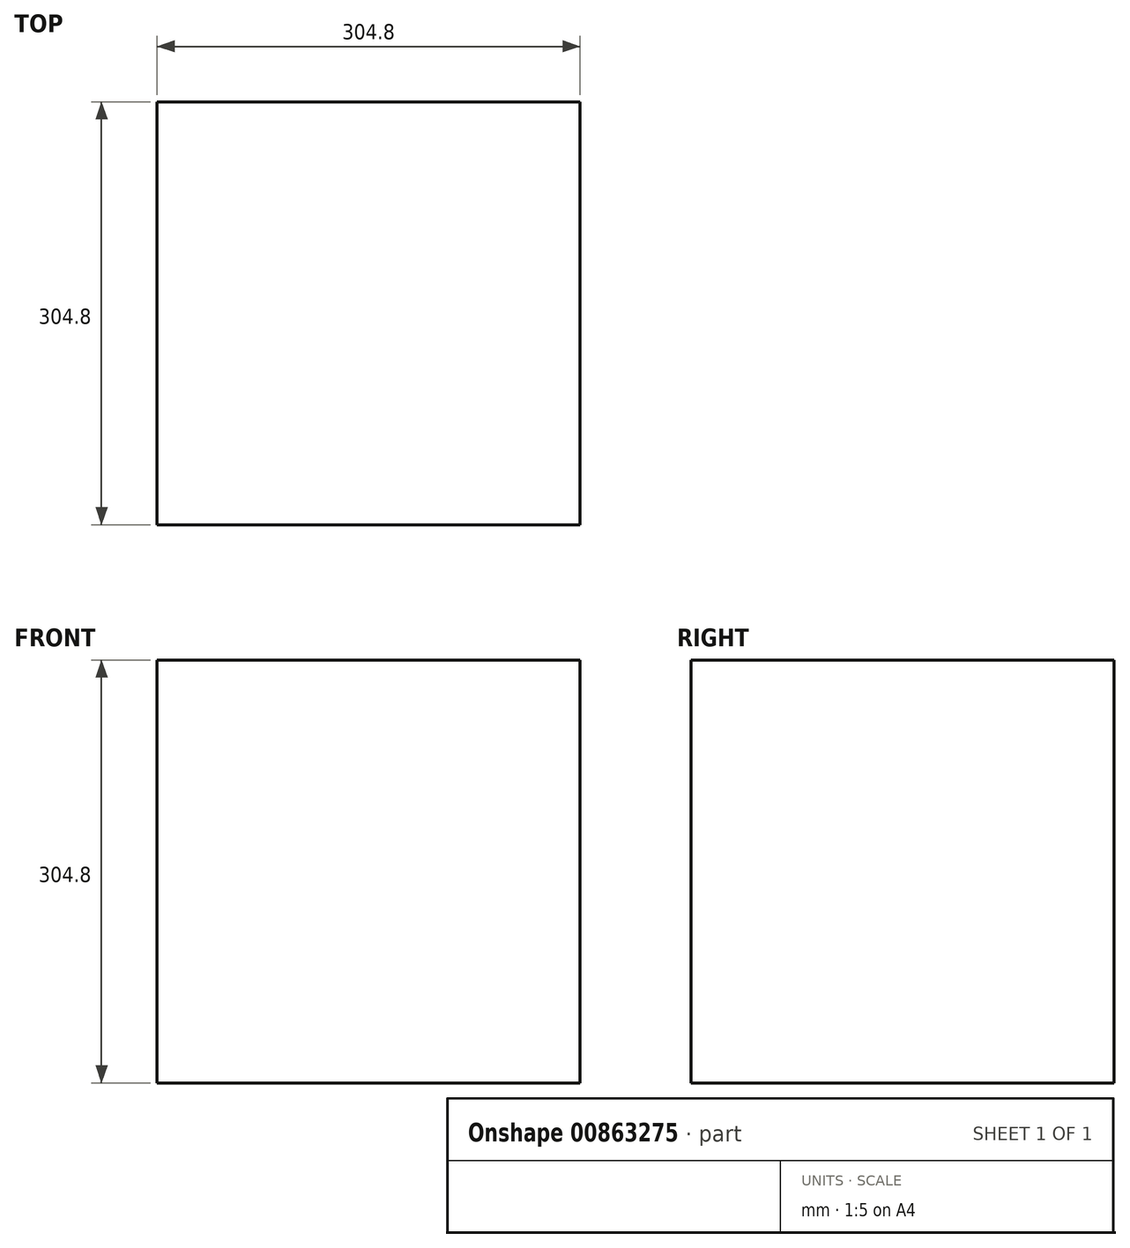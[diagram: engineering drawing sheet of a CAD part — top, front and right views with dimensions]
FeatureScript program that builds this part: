
annotation { "Feature Type Name" : "Feature", "Feature Type Description" : "" }
export const myFeature = defineFeature(function(context is Context, id is Id, definition is map)
    precondition{}
    {
        {
            var Q0;
            Q0=qCreatedBy(makeId("Front.planeOp"),FACE);
            var sketch = newSketch(context, id + "F0", { "sketchPlane" : qUnion([Q0])});
            skLineSegment(sketch, "E0.bottom", {"start": v(0, 0) * mm, "end": v(304.8, 0) * mm});
            skLineSegment(sketch, "E0.top", {"start": v(0, 304.8) * mm, "end": v(304.8, 304.8) * mm});
            skLineSegment(sketch, "E0.left", {"start": v(0, 0) * mm, "end": v(0, 304.8) * mm});
            skLineSegment(sketch, "E0.right", {"start": v(304.8, 0) * mm, "end": v(304.8, 304.8) * mm});
            skSolve(sketch);
        }
        {
            var Q0;
            Q0=makeQuery(id+"F0.imprint","IMPRINT",FACE,{"disambiguationData":[TD([[makeQuery(id+"F0.imprint","IMPRINT",EDGE,{"derivedFrom":sQuery(id+"F0.wireOp",EDGE,"E0.bottom")}),1.0]])]});
            extrude(context, id + "F1", {"entities" : qUnion([Q0]), "depth" : 304.8 * mm, "offsetDistance" : 30.48 * mm});
        }
    });
